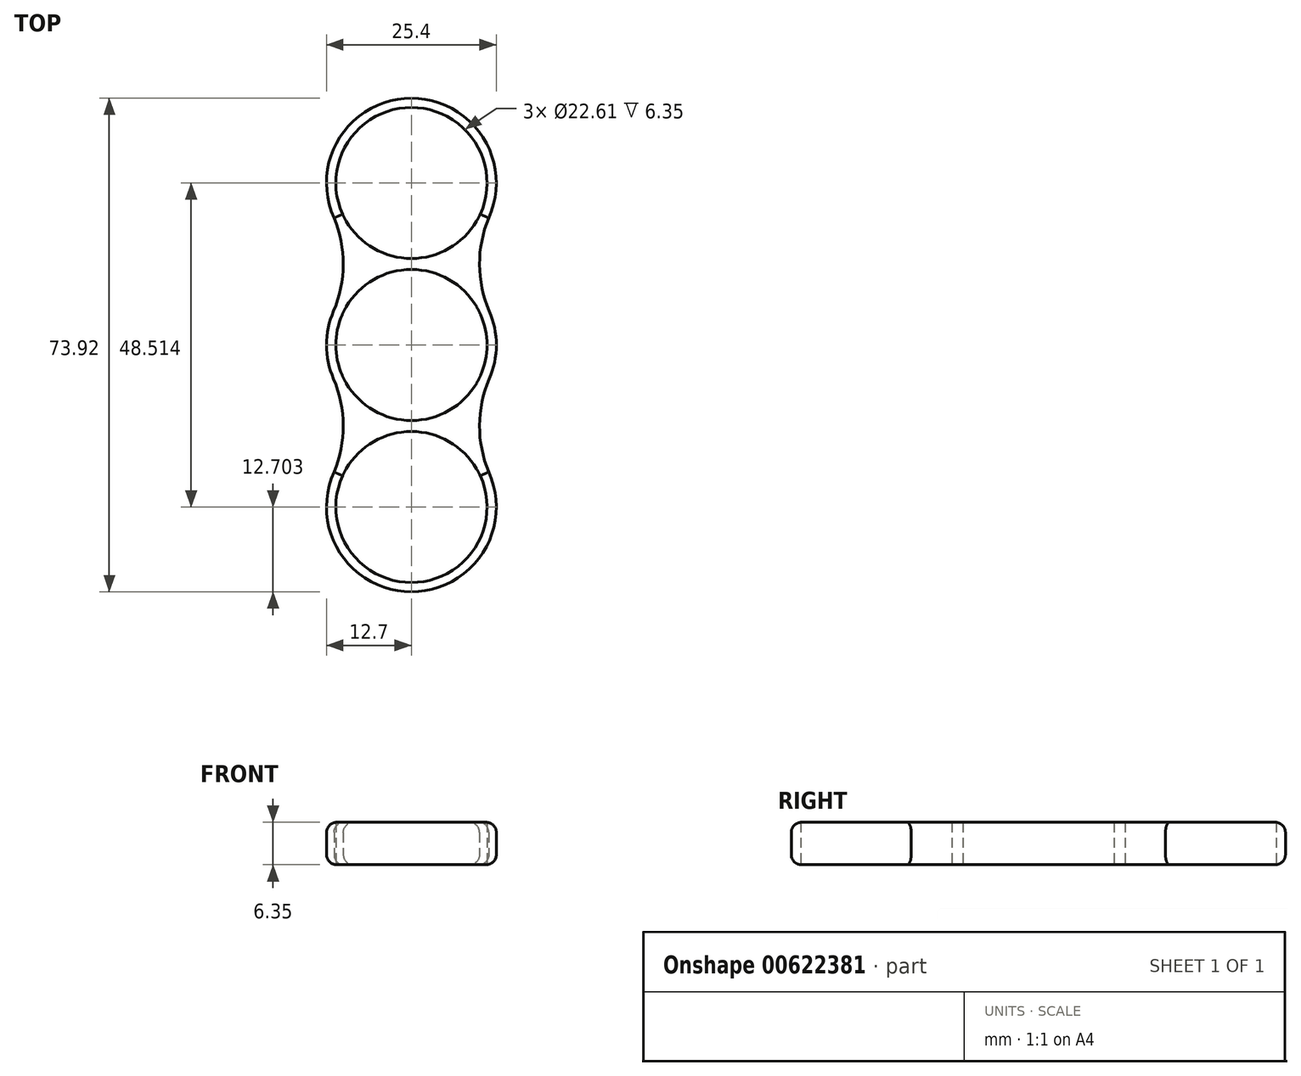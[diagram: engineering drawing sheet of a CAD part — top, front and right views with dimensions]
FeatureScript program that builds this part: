
annotation { "Feature Type Name" : "Feature", "Feature Type Description" : "" }
export const myFeature = defineFeature(function(context is Context, id is Id, definition is map)
    precondition{}
    {
        {
            var Q0;
            Q0=qCreatedBy(makeId("Top.planeOp"),FACE);
            var sketch = newSketch(context, id + "F0", { "sketchPlane" : qUnion([Q0])});
            skCircle(sketch, "E0", {"center": v(0, 0) * mm, "radius": 11.3 * mm});
            skCircle(sketch, "E1", {"center": v(0, 24.26) * mm, "radius": 11.3 * mm});
            skCircle(sketch, "E2.MirrorC", {"center": v(0, -24.26) * mm, "radius": 11.3 * mm});
            skPoint(sketch, "E3.MirrorCS.end.orphan", {"position": v(11.57, 21.83) * mm});
            skPoint(sketch, "E3.MirrorCS.start.orphan", {"position": v(11.67, 9.8) * mm});
            skPoint(sketch, "E4.MirrorCS.end.orphan", {"position": v(-11.57, 21.83) * mm});
            skPoint(sketch, "E4.MirrorCS.start.orphan", {"position": v(-11.67, 9.8) * mm});
            skPoint(sketch, "E5.MirrorCS.end.orphan", {"position": v(-11.57, -21.83) * mm});
            skPoint(sketch, "E5.MirrorCS.start.orphan", {"position": v(-11.67, -9.8) * mm});
            skPoint(sketch, "E6.end.orphan", {"position": v(11.57, -21.83) * mm});
            skPoint(sketch, "E6.start.orphan", {"position": v(11.67, -9.8) * mm});
            skArc(sketch, "E7", {"start": v(11.57, 19.02) * mm, "mid": v(0, 36.96) * mm, "end": v(-11.57, 19.02) * mm});
            skArc(sketch, "E8", {"start": v(-11.64, 5.08) * mm, "mid": v(-12.7, 0) * mm, "end": v(-11.64, -5.08) * mm});
            skArc(sketch, "E9", {"start": v(-11.57, -19.02) * mm, "mid": v(0, -36.96) * mm, "end": v(11.57, -19.02) * mm});
            skArc(sketch, "E10.trimOffspring", {"start": v(11.64, -5.08) * mm, "mid": v(12.7, 0) * mm, "end": v(11.64, 5.08) * mm});
            skArc(sketch, "E11", {"start": v(11.67, -5) * mm, "mid": v(10.2, -12) * mm, "end": v(11.57, -19.02) * mm});
            skArc(sketch, "E12.MirrorCS", {"start": v(-11.67, -5) * mm, "mid": v(-10.2, -12) * mm, "end": v(-11.57, -19.02) * mm});
            skArc(sketch, "E13.MirrorCS", {"start": v(11.67, 5) * mm, "mid": v(10.2, 12) * mm, "end": v(11.57, 19.02) * mm});
            skArc(sketch, "E14.MirrorCS", {"start": v(-11.67, 5) * mm, "mid": v(-10.2, 12) * mm, "end": v(-11.57, 19.02) * mm});
            skSolve(sketch);
        }
        {
            var Q0;
            Q0 = qSketchRegion(id + "F0", true);
            extrude(context, id + "F1", {"entities" : qUnion([Q0]), "depth" : 6.35 * mm, "offsetDistance" : 25.4 * mm});
        }
        {
            var Q0;
            Q0=makeQuery(id+"F1.opExtrude","CAP_EDGE",EDGE,{"disambiguationData":[OSD([sQuery(id+"F0.wireOp",EDGE,"E8")])],"isStart":false});
            var Q1;
            Q1=makeQuery(id+"F1.opExtrude","CAP_EDGE",EDGE,{"disambiguationData":[OSD([sQuery(id+"F0.wireOp",EDGE,"E14.MirrorCS")])],"isStart":false});
            var Q2;
            Q2=makeQuery(id+"F1.opExtrude","CAP_EDGE",EDGE,{"disambiguationData":[OSD([sQuery(id+"F0.wireOp",EDGE,"E7")])],"isStart":false});
            var Q3;
            Q3=makeQuery(id+"F1.opExtrude","CAP_EDGE",EDGE,{"disambiguationData":[OSD([sQuery(id+"F0.wireOp",EDGE,"E13.MirrorCS")])],"isStart":false});
            var Q4;
            Q4=makeQuery(id+"F1.opExtrude","CAP_EDGE",EDGE,{"disambiguationData":[OSD([sQuery(id+"F0.wireOp",EDGE,"E10.trimOffspring")])],"isStart":false});
            var Q5;
            Q5=makeQuery(id+"F1.opExtrude","CAP_EDGE",EDGE,{"disambiguationData":[OSD([sQuery(id+"F0.wireOp",EDGE,"E11")])],"isStart":false});
            var Q6;
            Q6=makeQuery(id+"F1.opExtrude","CAP_EDGE",EDGE,{"disambiguationData":[OSD([sQuery(id+"F0.wireOp",EDGE,"E9")])],"isStart":false});
            var Q7;
            Q7=makeQuery(id+"F1.opExtrude","CAP_EDGE",EDGE,{"disambiguationData":[OSD([sQuery(id+"F0.wireOp",EDGE,"E12.MirrorCS")])],"isStart":false});
            var Q8;
            Q8=makeQuery(id+"F1.opExtrude","CAP_EDGE",EDGE,{"disambiguationData":[OSD([sQuery(id+"F0.wireOp",EDGE,"E7")])],"isStart":true});
            var Q9;
            Q9=makeQuery(id+"F1.opExtrude","CAP_EDGE",EDGE,{"disambiguationData":[OSD([sQuery(id+"F0.wireOp",EDGE,"E14.MirrorCS")])],"isStart":true});
            var Q10;
            Q10=makeQuery(id+"F1.opExtrude","CAP_EDGE",EDGE,{"disambiguationData":[OSD([sQuery(id+"F0.wireOp",EDGE,"E8")])],"isStart":true});
            var Q11;
            Q11=makeQuery(id+"F1.opExtrude","CAP_EDGE",EDGE,{"disambiguationData":[OSD([sQuery(id+"F0.wireOp",EDGE,"E12.MirrorCS")])],"isStart":true});
            var Q12;
            Q12=makeQuery(id+"F1.opExtrude","CAP_EDGE",EDGE,{"disambiguationData":[OSD([sQuery(id+"F0.wireOp",EDGE,"E9")])],"isStart":true});
            var Q13;
            Q13=makeQuery(id+"F1.opExtrude","CAP_EDGE",EDGE,{"disambiguationData":[OSD([sQuery(id+"F0.wireOp",EDGE,"E11")])],"isStart":true});
            var Q14;
            Q14=makeQuery(id+"F1.opExtrude","CAP_EDGE",EDGE,{"disambiguationData":[OSD([sQuery(id+"F0.wireOp",EDGE,"E10.trimOffspring")])],"isStart":true});
            var Q15;
            Q15=makeQuery(id+"F1.opExtrude","CAP_EDGE",EDGE,{"disambiguationData":[OSD([sQuery(id+"F0.wireOp",EDGE,"E13.MirrorCS")])],"isStart":true});
            fillet(context, id + "F2", {"entities" : qUnion([Q0, Q1, Q2, Q3, Q4, Q5, Q6, Q7, Q8, Q9, Q10, Q11, Q12, Q13, Q14, Q15]), "radius" : 1.52 * mm, "tangentPropagation" : true, "allowEdgeOverflow" : false});
        }
    });
